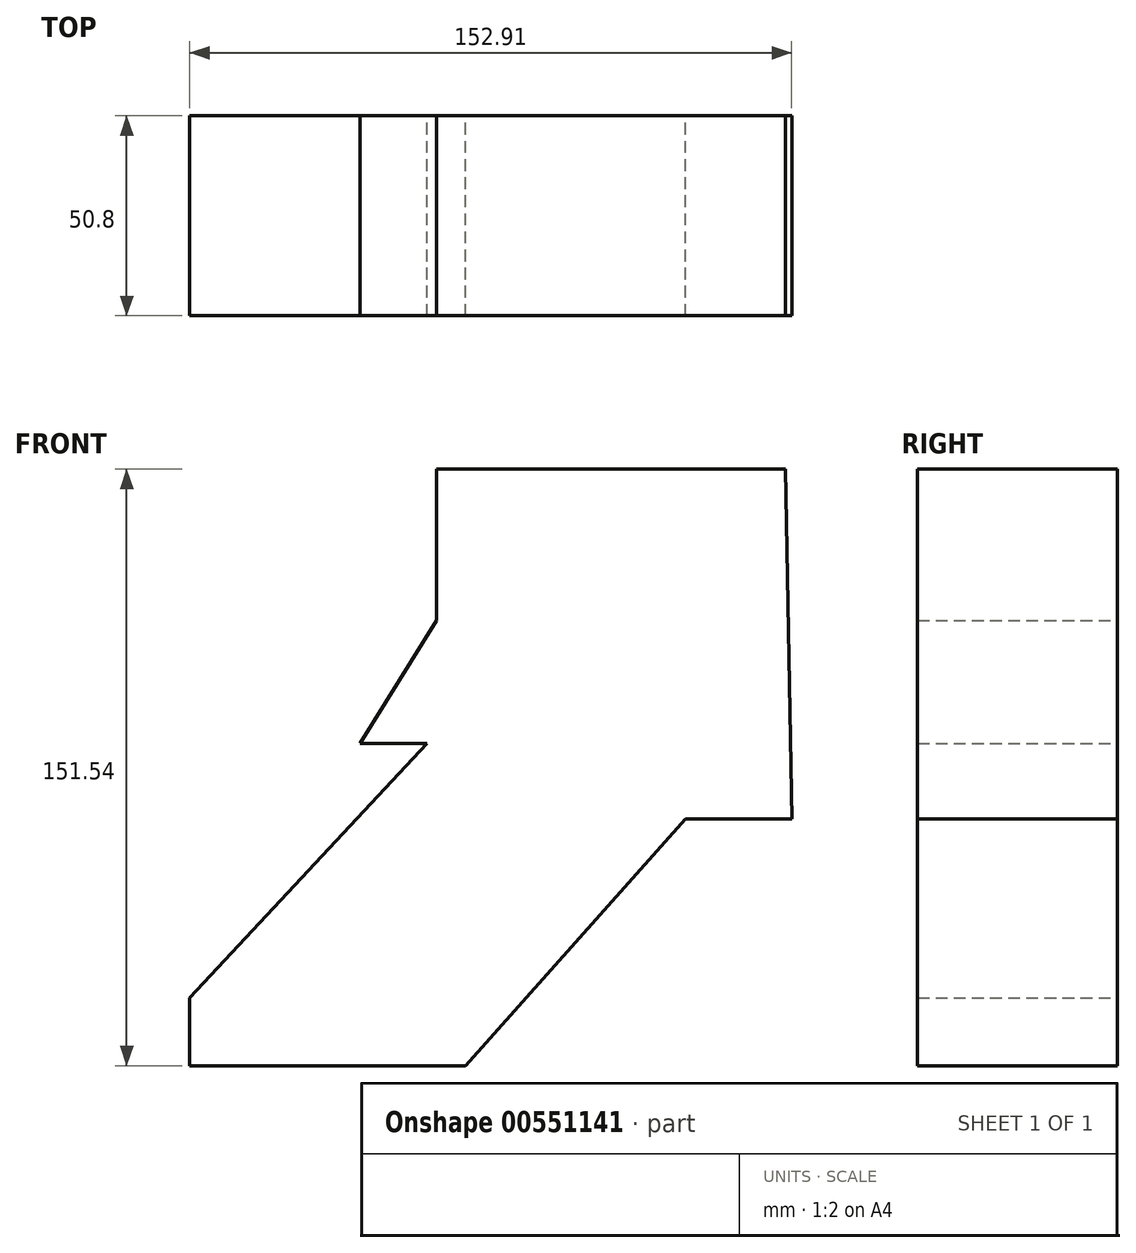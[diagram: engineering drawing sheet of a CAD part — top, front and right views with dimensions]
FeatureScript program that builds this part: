
annotation { "Feature Type Name" : "Feature", "Feature Type Description" : "" }
export const myFeature = defineFeature(function(context is Context, id is Id, definition is map)
    precondition{}
    {
        {
            var Q0;
            Q0=qCreatedBy(makeId("Front.planeOp"),FACE);
            var sketch = newSketch(context, id + "F0", { "sketchPlane" : qUnion([Q0])});
            skLineSegment(sketch, "E0", {"start": v(-76.3, -58.5) * mm, "end": v(-16, 6.12) * mm});
            skLineSegment(sketch, "E1", {"start": v(-16, 6.12) * mm, "end": v(-33.04, 6.12) * mm});
            skLineSegment(sketch, "E2", {"start": v(-33.04, 6.12) * mm, "end": v(-13.66, 37.44) * mm});
            skLineSegment(sketch, "E3", {"start": v(-13.66, 37.44) * mm, "end": v(-13.66, 75.82) * mm});
            skLineSegment(sketch, "E4", {"start": v(-13.66, 75.82) * mm, "end": v(75.04, 75.82) * mm});
            skLineSegment(sketch, "E5", {"start": v(75.04, 75.82) * mm, "end": v(76.6, -13.07) * mm});
            skLineSegment(sketch, "E6", {"start": v(76.6, -13.07) * mm, "end": v(49.58, -13.07) * mm});
            skLineSegment(sketch, "E7", {"start": v(49.58, -13.07) * mm, "end": v(-6.22, -75.72) * mm});
            skLineSegment(sketch, "E8", {"start": v(-6.22, -75.72) * mm, "end": v(-76.3, -75.72) * mm});
            skLineSegment(sketch, "E9", {"start": v(-76.3, -75.72) * mm, "end": v(-76.3, -58.5) * mm});
            skSolve(sketch);
        }
        {
            var Q0;
            Q0=makeQuery(id+"F0.imprint","IMPRINT",FACE,{"disambiguationData":[TD([[makeQuery(id+"F0.imprint","IMPRINT",EDGE,{"derivedFrom":sQuery(id+"F0.wireOp",EDGE,"E0")}),-1.0]])]});
            extrude(context, id + "F1", {"entities" : qUnion([Q0]), "depth" : 50.8 * mm, "offsetDistance" : 25.4 * mm});
        }
    });
